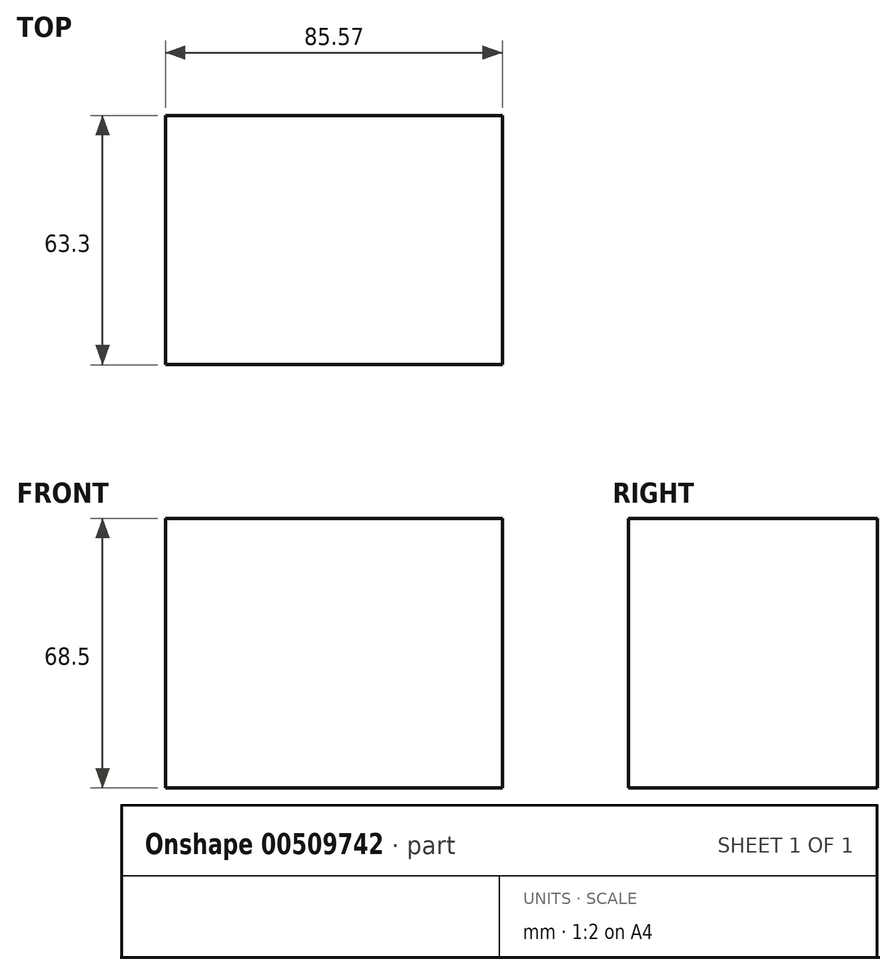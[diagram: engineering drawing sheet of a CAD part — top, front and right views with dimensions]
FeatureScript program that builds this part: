
annotation { "Feature Type Name" : "Feature", "Feature Type Description" : "" }
export const myFeature = defineFeature(function(context is Context, id is Id, definition is map)
    precondition{}
    {
        {
            var Q0;
            Q0=qCreatedBy(makeId("Top.planeOp"),FACE);
            var sketch = newSketch(context, id + "F0", { "sketchPlane" : qUnion([Q0])});
            skLineSegment(sketch, "E0.bottom", {"start": v(-108.44, -26.54) * mm, "end": v(-22.87, -26.54) * mm});
            skLineSegment(sketch, "E0.top", {"start": v(-108.44, -89.84) * mm, "end": v(-22.87, -89.84) * mm});
            skLineSegment(sketch, "E0.left", {"start": v(-108.44, -26.54) * mm, "end": v(-108.44, -89.84) * mm});
            skLineSegment(sketch, "E0.right", {"start": v(-22.87, -26.54) * mm, "end": v(-22.87, -89.84) * mm});
            skSolve(sketch);
        }
        {
            var Q0;
            Q0=makeQuery(id+"F0.imprint","IMPRINT",FACE,{"disambiguationData":[TD([[makeQuery(id+"F0.imprint","IMPRINT",EDGE,{"derivedFrom":sQuery(id+"F0.wireOp",EDGE,"E0.bottom")}),-1.0]])]});
            extrude(context, id + "F1", {"entities" : qUnion([Q0]), "depth" : 68.5 * mm});
        }
    });
